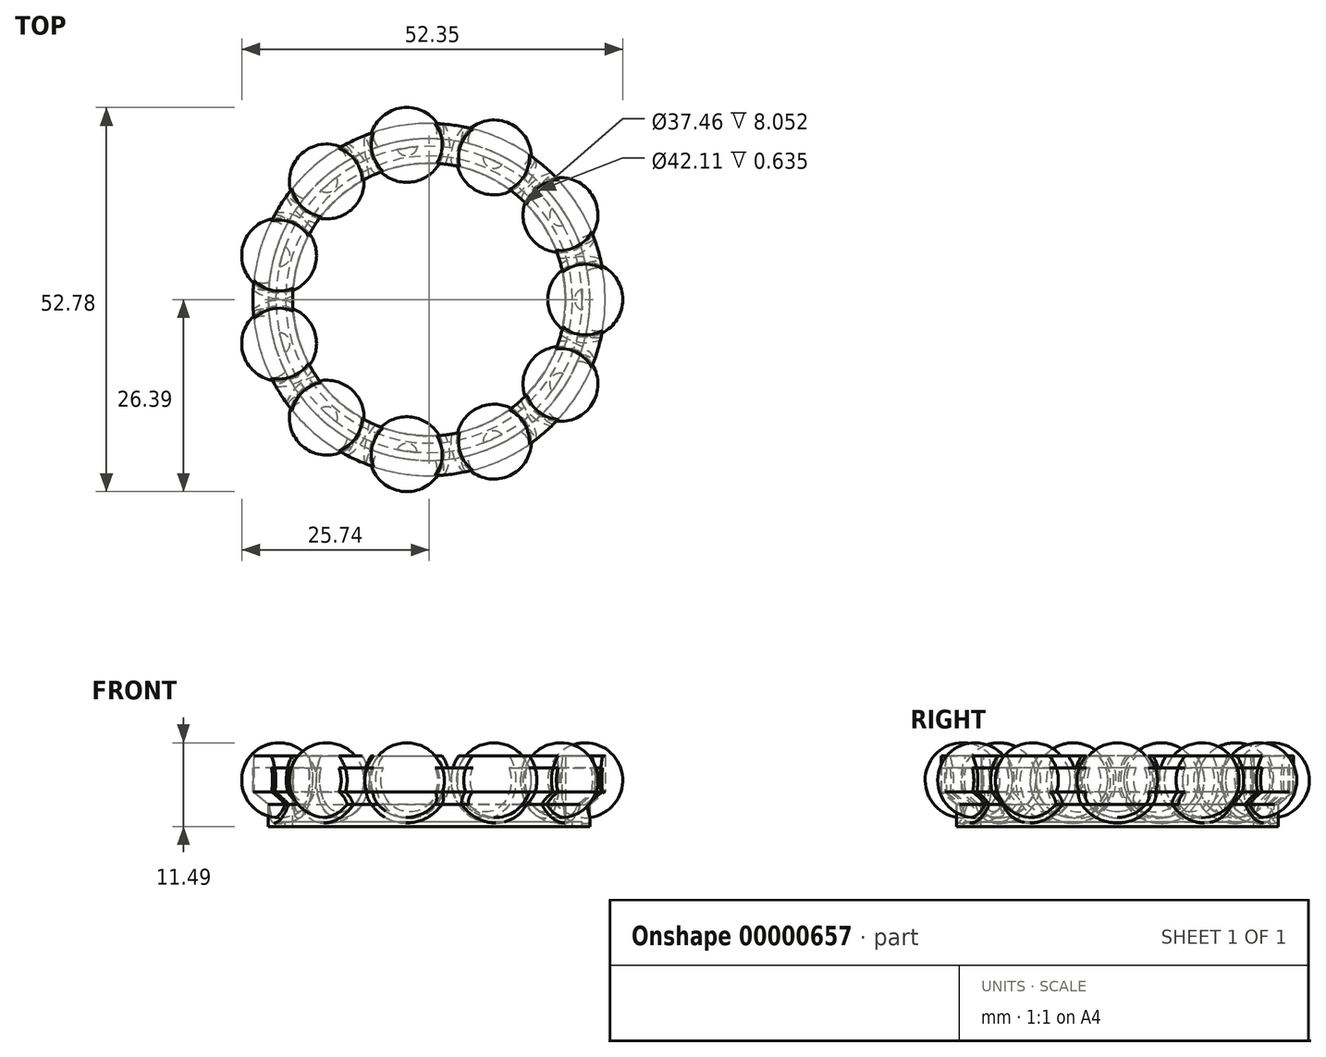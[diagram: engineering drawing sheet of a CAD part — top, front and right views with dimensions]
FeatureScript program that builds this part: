
annotation { "Feature Type Name" : "Feature", "Feature Type Description" : "" }
export const myFeature = defineFeature(function(context is Context, id is Id, definition is map)
    precondition{}
    {
        {
            var Q0;
            Q0=qCreatedBy(makeId("Front.planeOp"),FACE);
            var sketch = newSketch(context, id + "F0", { "sketchPlane" : qUnion([Q0])});
            skLineSegment(sketch, "E0", {"start": v(0, 0) * mm, "end": v(0, -9.7) * mm, "construction": true});
            skLineSegment(sketch, "E1", {"start": v(18.73, 0) * mm, "end": v(18.73, -9.7) * mm});
            skLineSegment(sketch, "E2", {"start": v(18.73, -9.7) * mm, "end": v(19.72, -9.7) * mm});
            skLineSegment(sketch, "E3", {"start": v(22.1, -9.7) * mm, "end": v(22.1, -6.65) * mm});
            skLineSegment(sketch, "E4", {"start": v(22.1, -6.65) * mm, "end": v(24.2, -4.95) * mm});
            skLineSegment(sketch, "E5", {"start": v(24.2, -4.95) * mm, "end": v(24.2, 0) * mm});
            skLineSegment(sketch, "E6", {"start": v(24.2, 0) * mm, "end": v(18.73, 0) * mm});
            skLineSegment(sketch, "E7.0.MirrorCS", {"start": v(-24.2, 0) * mm, "end": v(-18.73, 0) * mm, "construction": true});
            skLineSegment(sketch, "E7.1.MirrorCS", {"start": v(-22.1, -6.65) * mm, "end": v(-24.2, -4.95) * mm, "construction": true});
            skLineSegment(sketch, "E7.2.MirrorCS", {"start": v(-18.73, 0) * mm, "end": v(-18.73, -9.7) * mm, "construction": true});
            skLineSegment(sketch, "E7.3.MirrorCS", {"start": v(-22.1, -9.7) * mm, "end": v(-22.1, -6.65) * mm, "construction": true});
            skLineSegment(sketch, "E7.4.MirrorCS", {"start": v(-18.73, -9.7) * mm, "end": v(-22.1, -9.7) * mm, "construction": true});
            skLineSegment(sketch, "E7.5.MirrorCS", {"start": v(-24.2, -4.95) * mm, "end": v(-24.2, 0) * mm, "construction": true});
            skLineSegment(sketch, "E8", {"start": v(18.73, -1.65) * mm, "end": v(24.2, -1.65) * mm});
            skLineSegment(sketch, "E9", {"start": v(19.72, -9.7) * mm, "end": v(19.72, -9.07) * mm});
            skLineSegment(sketch, "E10", {"start": v(19.72, -9.07) * mm, "end": v(21.06, -9.07) * mm});
            skLineSegment(sketch, "E11", {"start": v(21.06, -9.07) * mm, "end": v(21.06, -9.7) * mm});
            skLineSegment(sketch, "E12.trimOffspring", {"start": v(21.06, -9.7) * mm, "end": v(22.1, -9.7) * mm});
            skSolve(sketch);
        }
        {
            var Q0;
            {var subQ3=sQuery(id+"F0.wireOp",EDGE,"E2");Q0=makeQuery(id+"F0.imprint","IMPRINT",FACE,{"disambiguationData":[TD([[makeQuery(id+"F0.imprint","IMPRINT",EDGE,{"derivedFrom":subQ3}),1.0]])]});}
            var Q1;
            Q1=sQuery(id+"F0.wireOp",EDGE,"E0");
            revolve(context, id + "F1", {"entities" : qUnion([Q0]), "axis" : qUnion([Q1]), "revolveType" : RevolveType.FULL});
        }
        {
            var Q0;
            Q0=qCreatedBy(makeId("Front.planeOp"),FACE);
            var sketch = newSketch(context, id + "F2", { "sketchPlane" : qUnion([Q0])});
            skArc(sketch, "E13", {"start": v(21.46, -8.5) * mm, "mid": v(26.6, -3.35) * mm, "end": v(21.46, 1.8) * mm});
            skLineSegment(sketch, "E14", {"start": v(21.46, 1.8) * mm, "end": v(21.46, -8.5) * mm});
            skArc(sketch, "E15", {"start": v(21.46, -9.26) * mm, "mid": v(27.37, -3.35) * mm, "end": v(21.46, 2.55) * mm});
            skLineSegment(sketch, "E16", {"start": v(21.46, 1.8) * mm, "end": v(21.46, 2.55) * mm});
            skLineSegment(sketch, "E17", {"start": v(21.46, -8.5) * mm, "end": v(21.46, -9.26) * mm});
            skLineSegment(sketch, "E18", {"start": v(21.46, -3.35) * mm, "end": v(0, -3.35) * mm, "construction": true});
            skLineSegment(sketch, "E19", {"start": v(0, -3.35) * mm, "end": v(0, 0) * mm, "construction": true});
            skSolve(sketch);
        }
        {
            var Q0;
            Q0=makeQuery(id+"F2.imprint","IMPRINT",FACE,{"disambiguationData":[TD([[makeQuery(id+"F2.imprint","IMPRINT",EDGE,{"derivedFrom":sQuery(id+"F2.wireOp",EDGE,"E13")}),1.0]])]});
            var Q1;
            Q1=makeQuery(id+"F2.imprint","IMPRINT",FACE,{"disambiguationData":[TD([[makeQuery(id+"F2.imprint","IMPRINT",EDGE,{"derivedFrom":sQuery(id+"F2.wireOp",EDGE,"E13")}),-1.0]])]});
            var Q2;
            Q2=sQuery(id+"F2.wireOp",EDGE,"E14");
            revolve(context, id + "F3", {"entities" : qUnion([Q0, Q1]), "axis" : qUnion([Q2]), "revolveType" : RevolveType.FULL});
        }
        {
            var Q0;
            Q0=makeQuery(id+"F3.opRevolve","SWEPT_BODY",BODY,{"disambiguationData":[OSD([sQuery(id+"F2.wireOp",EDGE,"E14"),sQuery(id+"F2.wireOp",EDGE,"E15"),sQuery(id+"F2.wireOp",EDGE,"E16"),sQuery(id+"F2.wireOp",EDGE,"E17")])]});
            var Q1;
            Q1=sQuery(id+"F0.wireOp",EDGE,"E0");
            circularPattern(context, id + "F4", {"entities" : qUnion([Q0]), "axis" : qUnion([Q1]), "angle" : 360 * degree, "instanceCount" : 11, "equalSpace" : true});
        }
        {
            var Q0;
            {var subQ4=sQuery(id+"F0.wireOp",EDGE,"E6");var subQ8=sQuery(id+"F0.wireOp",EDGE,"E2");Q0=qUnion([makeQuery(id+"F0.imprint","IMPRINT",FACE,{"disambiguationData":[TD([[makeQuery(id+"F0.imprint","IMPRINT",EDGE,{"derivedFrom":subQ4}),1.0]])]}),makeQuery(id+"F0.imprint","IMPRINT",FACE,{"disambiguationData":[TD([[makeQuery(id+"F0.imprint","IMPRINT",EDGE,{"derivedFrom":subQ8}),1.0]])]})]);}
            var Q1;
            Q1=sQuery(id+"F0.wireOp",EDGE,"E0");
            revolve(context, id + "F5", {"operationType" : NewBodyOperationType.INTERSECT, "entities" : qUnion([Q0]), "axis" : qUnion([Q1]), "revolveType" : RevolveType.FULL, "oppositeDirection" : true});
        }
        {
            var Q0;
            Q0=makeQuery(id+"F2.imprint","IMPRINT",FACE,{"disambiguationData":[TD([[makeQuery(id+"F2.imprint","IMPRINT",EDGE,{"derivedFrom":sQuery(id+"F2.wireOp",EDGE,"E13")}),1.0]])]});
            var Q1;
            Q1=sQuery(id+"F2.wireOp",EDGE,"E14");
            revolve(context, id + "F6", {"entities" : qUnion([Q0]), "axis" : qUnion([Q1]), "revolveType" : RevolveType.FULL});
        }
        {
            var Q0;
            Q0=makeQuery(id+"F6.opRevolve","SWEPT_BODY",BODY,{"disambiguationData":[OSD([sQuery(id+"F2.wireOp",EDGE,"E13"),sQuery(id+"F2.wireOp",EDGE,"E14")])]});
            var Q1;
            Q1=sQuery(id+"F0.wireOp",EDGE,"E0");
            circularPattern(context, id + "F7", {"entities" : qUnion([Q0]), "axis" : qUnion([Q1]), "angle" : 360 * degree, "instanceCount" : 11, "equalSpace" : true});
        }
        {
            var Q0;
            Q0=makeQuery(id+"F6.opRevolve","SWEPT_BODY",BODY,{"disambiguationData":[OSD([sQuery(id+"F2.wireOp",EDGE,"E13"),sQuery(id+"F2.wireOp",EDGE,"E14")])]});
            var Q1;
            Q1=makeQuery(id+"F7.opPattern","COPY",BODY,{"derivedFrom":makeQuery(id+"F6.opRevolve","SWEPT_BODY",BODY,{"disambiguationData":[OSD([sQuery(id+"F2.wireOp",EDGE,"E13"),sQuery(id+"F2.wireOp",EDGE,"E14")])]}),"instanceName":"1"});
            var Q2;
            Q2=makeQuery(id+"F7.opPattern","COPY",BODY,{"derivedFrom":makeQuery(id+"F6.opRevolve","SWEPT_BODY",BODY,{"disambiguationData":[OSD([sQuery(id+"F2.wireOp",EDGE,"E13"),sQuery(id+"F2.wireOp",EDGE,"E14")])]}),"instanceName":"2"});
            var Q3;
            Q3=makeQuery(id+"F7.opPattern","COPY",BODY,{"derivedFrom":makeQuery(id+"F6.opRevolve","SWEPT_BODY",BODY,{"disambiguationData":[OSD([sQuery(id+"F2.wireOp",EDGE,"E13"),sQuery(id+"F2.wireOp",EDGE,"E14")])]}),"instanceName":"3"});
            var Q4;
            Q4=makeQuery(id+"F7.opPattern","COPY",BODY,{"derivedFrom":makeQuery(id+"F6.opRevolve","SWEPT_BODY",BODY,{"disambiguationData":[OSD([sQuery(id+"F2.wireOp",EDGE,"E13"),sQuery(id+"F2.wireOp",EDGE,"E14")])]}),"instanceName":"4"});
            var Q5;
            Q5=makeQuery(id+"F7.opPattern","COPY",BODY,{"derivedFrom":makeQuery(id+"F6.opRevolve","SWEPT_BODY",BODY,{"disambiguationData":[OSD([sQuery(id+"F2.wireOp",EDGE,"E13"),sQuery(id+"F2.wireOp",EDGE,"E14")])]}),"instanceName":"5"});
            var Q6;
            Q6=makeQuery(id+"F7.opPattern","COPY",BODY,{"derivedFrom":makeQuery(id+"F6.opRevolve","SWEPT_BODY",BODY,{"disambiguationData":[OSD([sQuery(id+"F2.wireOp",EDGE,"E13"),sQuery(id+"F2.wireOp",EDGE,"E14")])]}),"instanceName":"6"});
            var Q7;
            Q7=makeQuery(id+"F7.opPattern","COPY",BODY,{"derivedFrom":makeQuery(id+"F6.opRevolve","SWEPT_BODY",BODY,{"disambiguationData":[OSD([sQuery(id+"F2.wireOp",EDGE,"E13"),sQuery(id+"F2.wireOp",EDGE,"E14")])]}),"instanceName":"7"});
            var Q8;
            Q8=makeQuery(id+"F7.opPattern","COPY",BODY,{"derivedFrom":makeQuery(id+"F6.opRevolve","SWEPT_BODY",BODY,{"disambiguationData":[OSD([sQuery(id+"F2.wireOp",EDGE,"E13"),sQuery(id+"F2.wireOp",EDGE,"E14")])]}),"instanceName":"8"});
            var Q9;
            Q9=makeQuery(id+"F7.opPattern","COPY",BODY,{"derivedFrom":makeQuery(id+"F6.opRevolve","SWEPT_BODY",BODY,{"disambiguationData":[OSD([sQuery(id+"F2.wireOp",EDGE,"E13"),sQuery(id+"F2.wireOp",EDGE,"E14")])]}),"instanceName":"9"});
            var Q10;
            Q10=makeQuery(id+"F7.opPattern","COPY",BODY,{"derivedFrom":makeQuery(id+"F6.opRevolve","SWEPT_BODY",BODY,{"disambiguationData":[OSD([sQuery(id+"F2.wireOp",EDGE,"E13"),sQuery(id+"F2.wireOp",EDGE,"E14")])]}),"instanceName":"10"});
            var Q11;
            Q11=makeQuery(id+"F1.opRevolve","SWEPT_BODY",BODY,{"disambiguationData":[OSD([sQuery(id+"F0.wireOp",EDGE,"E1"),sQuery(id+"F0.wireOp",EDGE,"E2"),sQuery(id+"F0.wireOp",EDGE,"E3"),sQuery(id+"F0.wireOp",EDGE,"E4"),sQuery(id+"F0.wireOp",EDGE,"E5"),sQuery(id+"F0.wireOp",EDGE,"E8"),sQuery(id+"F0.wireOp",EDGE,"E9"),sQuery(id+"F0.wireOp",EDGE,"E10"),sQuery(id+"F0.wireOp",EDGE,"E11"),sQuery(id+"F0.wireOp",EDGE,"E12.trimOffspring")])]});
            booleanBodies(context, id + "F8", {"operationType" : BooleanOperationType.SUBTRACTION, "tools" : qUnion([Q0, Q1, Q2, Q3, Q4, Q5, Q6, Q7, Q8, Q9, Q10]), "targets" : qUnion([Q11]), "keepTools" : true});
        }
    });
